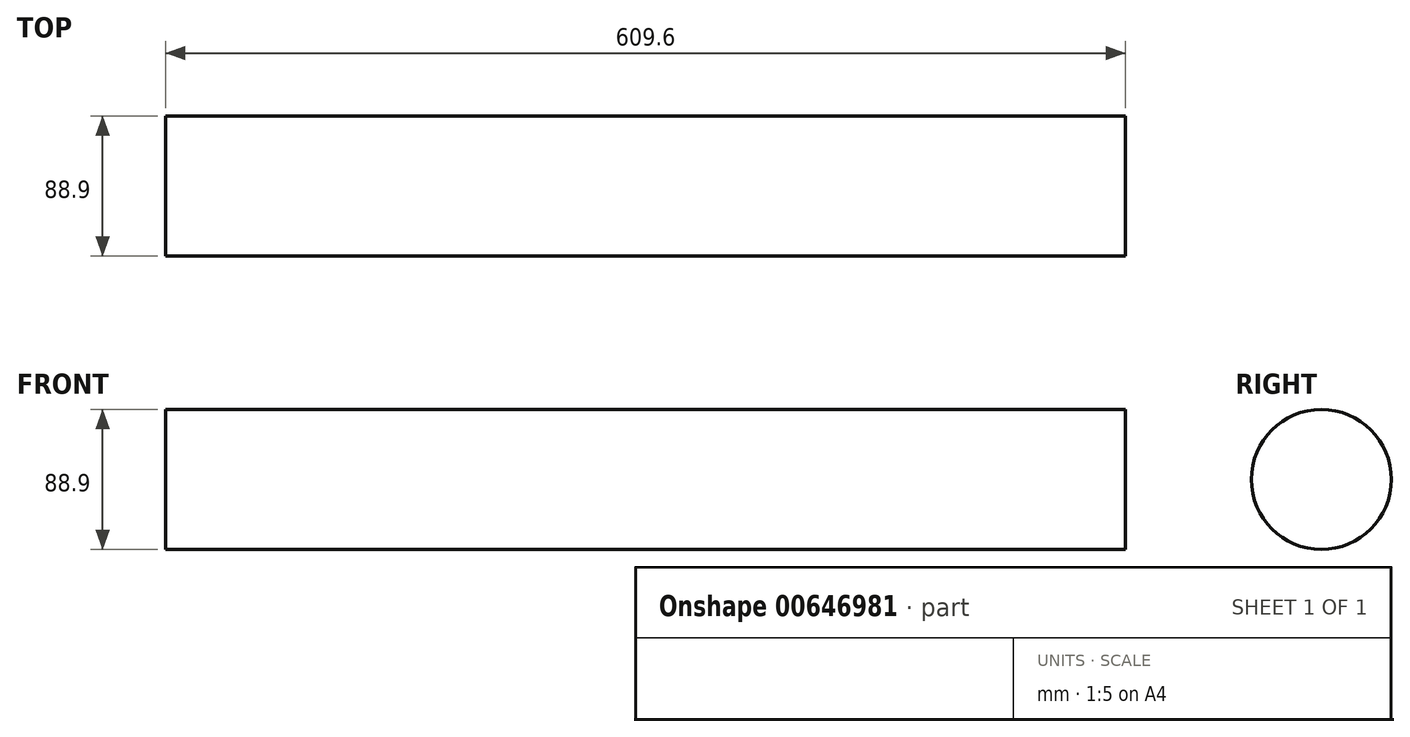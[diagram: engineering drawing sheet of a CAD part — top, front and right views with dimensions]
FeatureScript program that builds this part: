
annotation { "Feature Type Name" : "Feature", "Feature Type Description" : "" }
export const myFeature = defineFeature(function(context is Context, id is Id, definition is map)
    precondition{}
    {
        {
            var Q0;
            Q0=qCreatedBy(makeId("Right.planeOp"),FACE);
            var sketch = newSketch(context, id + "F0", { "sketchPlane" : qUnion([Q0])});
            skCircle(sketch, "E0", {"center": v(0, 0) * mm, "radius": 44.45 * mm});
            skSolve(sketch);
        }
        {
            var Q0;
            Q0 = qSketchRegion(id + "F0", true);
            var Q1;
            Q1=sQuery(id+"F0.wireOp",EDGE,"E0");
            extrude(context, id + "F1", {"entities" : qUnion([Q0]), "surfaceEntities" : qUnion([Q1]), "depth" : 304.8 * mm, "offsetDistance" : 25.4 * mm, "hasSecondDirection" : true, "secondDirectionOppositeDirection" : true, "secondDirectionDepth" : 304.8 * mm});
        }
    });
